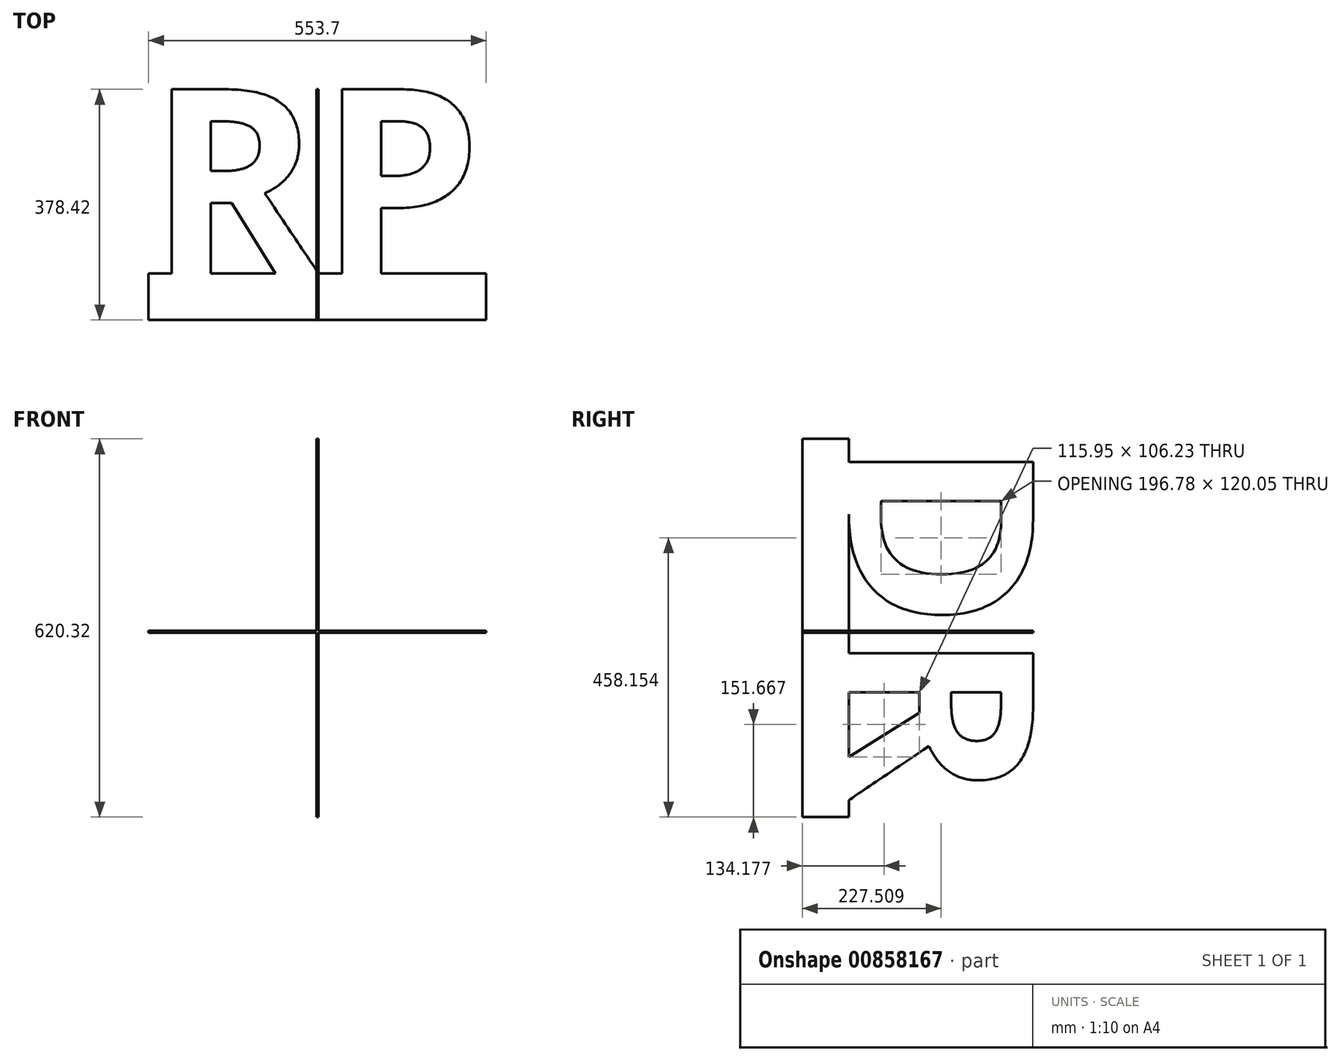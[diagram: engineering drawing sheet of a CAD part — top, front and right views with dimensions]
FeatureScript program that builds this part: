
annotation { "Feature Type Name" : "Feature", "Feature Type Description" : "" }
export const myFeature = defineFeature(function(context is Context, id is Id, definition is map)
    precondition{}
    {
        {
            var Q0;
            Q0=qCreatedBy(makeId("Top.planeOp"),FACE);
            var sketch = newSketch(context, id + "F0", { "sketchPlane" : qUnion([Q0])});
            skText(sketch, "E0", { "text": "RP", "fontName": "OpenSans-Bold.ttf"});
            skLineSegment(sketch, "E1.bottom", {"start": v(-276.85, 0) * mm, "end": v(276.85, 0) * mm});
            skLineSegment(sketch, "E1.top", {"start": v(-276.85, -76.2) * mm, "end": v(276.85, -76.2) * mm});
            skLineSegment(sketch, "E1.left", {"start": v(-276.85, 0) * mm, "end": v(-276.85, -76.2) * mm});
            skLineSegment(sketch, "E1.right", {"start": v(276.85, 0) * mm, "end": v(276.85, -76.2) * mm});
            const initialGuessF0  = {"E0": [-0.27685, 0, 1, 0, 0.3048]};
            skSetInitialGuess(sketch, initialGuessF0);
            skSolve(sketch);
        }
        {
            var Q0;
            Q0 = qSketchRegion(id + "F0", true);
            extrude(context, id + "F1", {"entities" : qUnion([Q0]), "endBound" : BoundingType.SYMMETRIC, "depth" : 3.17 * mm, "offsetDistance" : 25.4 * mm});
        }
        {
            var Q0;
            Q0=qCreatedBy(makeId("Right.planeOp"),FACE);
            var sketch = newSketch(context, id + "F2", { "sketchPlane" : qUnion([Q0])});
            skText(sketch, "E2", { "text": "DR", "fontName": "OpenSans-Bold.ttf"});
            skLineSegment(sketch, "E3.bottom", {"start": v(0, 316.5) * mm, "end": v(-76.2, 316.5) * mm});
            skLineSegment(sketch, "E3.top", {"start": v(0, -303.8) * mm, "end": v(-76.2, -303.8) * mm});
            skLineSegment(sketch, "E3.left", {"start": v(0, 316.5) * mm, "end": v(0, -303.8) * mm});
            skLineSegment(sketch, "E3.right", {"start": v(-76.2, 316.5) * mm, "end": v(-76.2, -303.8) * mm});
            const initialGuessF2  = {"E2": [0, 0.3165, 0, -1, 0.3048]};
            skSetInitialGuess(sketch, initialGuessF2);
            skSolve(sketch);
        }
        {
            var Q0;
            Q0 = qSketchRegion(id + "F2", true);
            extrude(context, id + "F3", {"entities" : qUnion([Q0]), "operationType" : NewBodyOperationType.ADD, "endBound" : BoundingType.SYMMETRIC, "depth" : 3.17 * mm, "offsetDistance" : 25.4 * mm});
        }
    });
